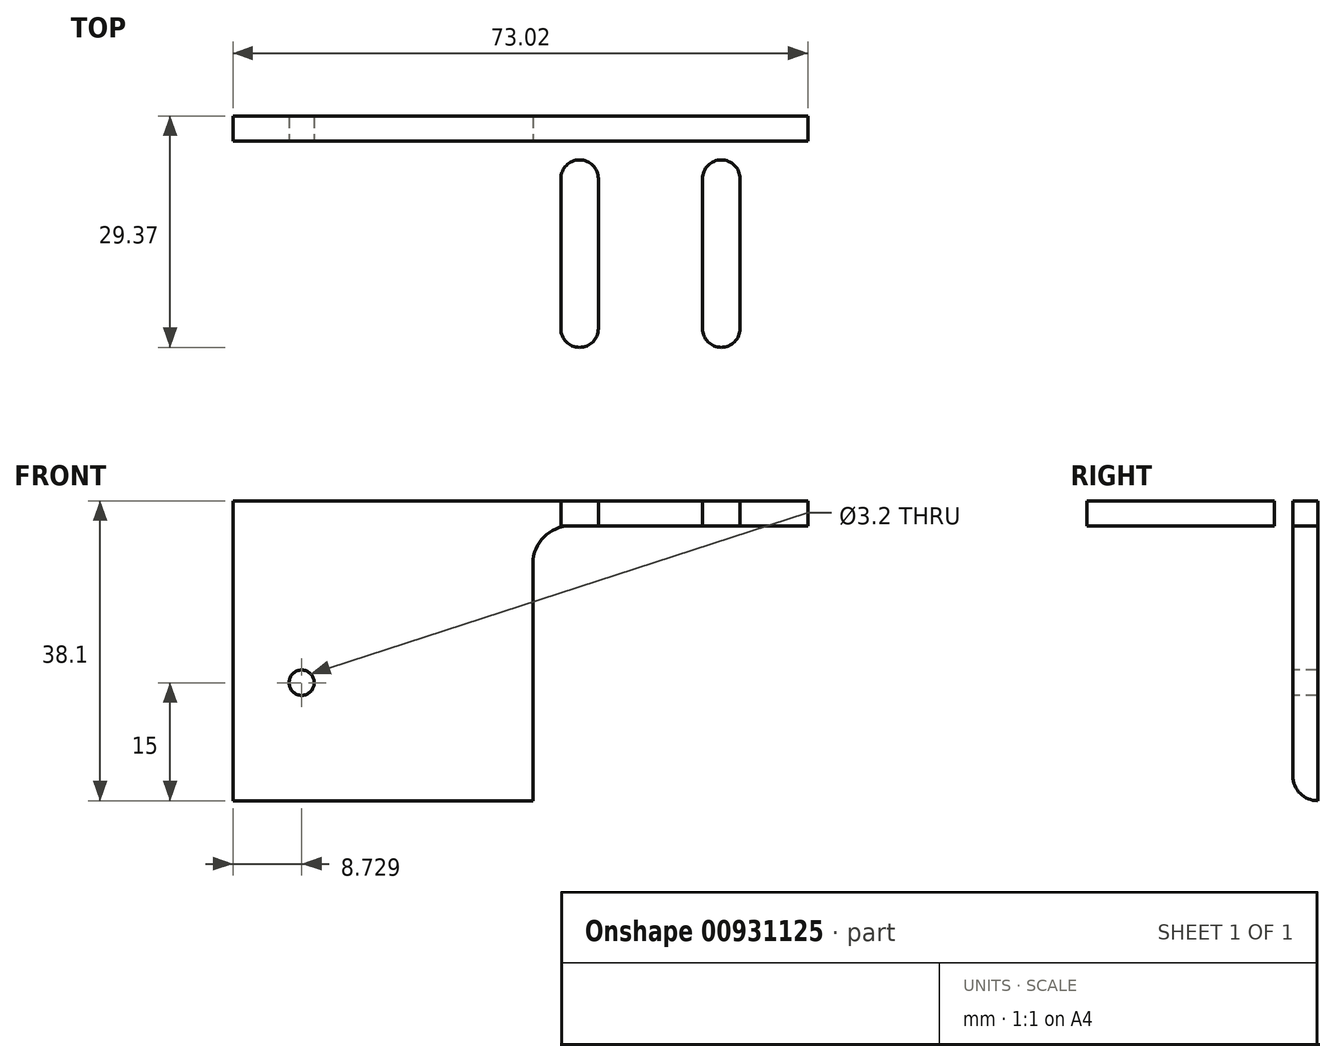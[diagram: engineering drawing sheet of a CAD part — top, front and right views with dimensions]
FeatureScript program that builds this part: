
annotation { "Feature Type Name" : "Feature", "Feature Type Description" : "" }
export const myFeature = defineFeature(function(context is Context, id is Id, definition is map)
    precondition{}
    {
        {
            var Q0;
            Q0=qCreatedBy(makeId("Front.planeOp"),FACE);
            var sketch = newSketch(context, id + "F0", { "sketchPlane" : qUnion([Q0])});
            skLineSegment(sketch, "E0.bottom", {"start": v(36.51, -19.05) * mm, "end": v(-36.51, -19.05) * mm});
            skLineSegment(sketch, "E0.top", {"start": v(36.51, 19.05) * mm, "end": v(-36.51, 19.05) * mm});
            skLineSegment(sketch, "E0.left", {"start": v(36.51, -19.05) * mm, "end": v(36.51, 19.05) * mm});
            skLineSegment(sketch, "E0.right", {"start": v(-36.51, -19.05) * mm, "end": v(-36.51, 19.05) * mm});
            skPoint(sketch, "E0.middle", {"position": v(0, 0) * mm});
            skSolve(sketch);
        }
        {
            var Q0;
            Q0=makeQuery(id+"F0.imprint","IMPRINT",FACE,{"disambiguationData":[TD([[makeQuery(id+"F0.imprint","IMPRINT",EDGE,{"derivedFrom":sQuery(id+"F0.wireOp",EDGE,"E0.bottom")}),-1.0]])]});
            extrude(context, id + "F1", {"entities" : qUnion([Q0]), "depth" : 3.17 * mm, "offsetDistance" : 25.4 * mm});
        }
        {
            var Q0;
            Q0=makeQuery(id+"F1.opExtrude","SWEPT_FACE",FACE,{"disambiguationData":[OSD([sQuery(id+"F0.wireOp",EDGE,"E0.top")])]});
            var sketch = newSketch(context, id + "F2", { "sketchPlane" : qUnion([Q0])});
            skLineSegment(sketch, "E1.bottom", {"start": v(-36.51, 0) * mm, "end": v(36.51, 0) * mm});
            skLineSegment(sketch, "E1.top", {"start": v(-36.51, -38.1) * mm, "end": v(36.51, -38.1) * mm});
            skLineSegment(sketch, "E1.left", {"start": v(-36.51, 0) * mm, "end": v(-36.51, -38.1) * mm});
            skLineSegment(sketch, "E1.right", {"start": v(36.51, 0) * mm, "end": v(36.51, -38.1) * mm});
            skSolve(sketch);
        }
        {
            var Q0;
            {var subQ0=sQuery(id+"F2.wireOp",EDGE,"E1.top");Q0=makeQuery(id+"F2.imprint","IMPRINT",FACE,{"disambiguationData":[TD([[makeQuery(id+"F2.imprint","IMPRINT",EDGE,{"derivedFrom":subQ0}),1.0]])]});}
            extrude(context, id + "F3", {"entities" : qUnion([Q0]), "operationType" : NewBodyOperationType.ADD, "oppositeDirection" : true, "depth" : 3.17 * mm, "offsetDistance" : 25.4 * mm});
        }
        {
            var Q0;
            Q0=makeQuery(id+"F1.opExtrude","CAP_FACE",FACE,{"disambiguationData":[OSD([sQuery(id+"F0.wireOp",EDGE,"E0.bottom"),sQuery(id+"F0.wireOp",EDGE,"E0.top"),sQuery(id+"F0.wireOp",EDGE,"E0.left"),sQuery(id+"F0.wireOp",EDGE,"E0.right")])],"isStart":false});
            var sketch = newSketch(context, id + "F4", { "sketchPlane" : qUnion([Q0])});
            skPoint(sketch, "E2", {"position": v(-27.78, -4.05) * mm});
            skSolve(sketch);
        }
        {
            var Q0;
            Q0=sQuery(id+"F4.wireOp",VERTEX,"E2");
            var Q1;
            Q1=makeQuery(id+"F1.opExtrude","SWEPT_BODY",BODY,{"disambiguationData":[OSD([sQuery(id+"F0.wireOp",EDGE,"E0.bottom"),sQuery(id+"F0.wireOp",EDGE,"E0.top"),sQuery(id+"F0.wireOp",EDGE,"E0.left"),sQuery(id+"F0.wireOp",EDGE,"E0.right")])]});
            hole(context, id + "F5", {"style" : HoleStyle.SIMPLE, "endStyle" : HoleEndStyle.BLIND, "standardTappedOrClearance" : lookupTablePath({ "fit" : "Close", "standard" : "ISO", "size" : "M3", "type" : "Clearance" }), "standardBlindInLast" : lookupTablePath({ "fit" : "Close", "standard" : "ISO", "engagement" : "75%", "pitch" : "0.5 mm", "size" : "M3", "type" : "Clearance & tapped" }), "holeDiameter" : 3.2 * mm, "majorDiameter" : 6.35 * mm, "holeDepth" : 34.92 * mm, "isTappedThrough" : true, "tappedDepth" : 7.9 * mm, "tapClearance" : 3, "startFromSketch" : true, "locations" : qUnion([Q0]), "scope" : qUnion([Q1])});
        }
        {
            var Q0;
            Q0=makeQuery(id+"F3.opExtrude","CAP_FACE",FACE,{"disambiguationData":[OSD([sQuery(id+"F0.wireOp",EDGE,"E0.top"),sQuery(id+"F2.wireOp",EDGE,"E1.top"),sQuery(id+"F2.wireOp",EDGE,"E1.left"),sQuery(id+"F2.wireOp",EDGE,"E1.right")])],"isStart":false});
            var sketch = newSketch(context, id + "F6", { "sketchPlane" : qUnion([Q0])});
            skLineSegment(sketch, "E3", {"start": v(25.51, 7.94) * mm, "end": v(25.51, 26.99) * mm});
            skLineSegment(sketch, "E4", {"start": v(7.51, 7.94) * mm, "end": v(7.51, 26.99) * mm});
            skArc(sketch, "E5.0.startCap", {"start": v(27.9, 7.94) * mm, "mid": v(25.51, 5.56) * mm, "end": v(23.13, 7.94) * mm});
            skArc(sketch, "E5.0.endCap", {"start": v(23.13, 26.99) * mm, "mid": v(25.51, 29.37) * mm, "end": v(27.9, 26.99) * mm});
            skLineSegment(sketch, "E5.0.left", {"start": v(23.13, 7.94) * mm, "end": v(23.13, 26.99) * mm});
            skLineSegment(sketch, "E5.0.right", {"start": v(27.9, 7.94) * mm, "end": v(27.9, 26.99) * mm});
            skArc(sketch, "E5.1.startCap", {"start": v(9.9, 7.94) * mm, "mid": v(7.51, 5.56) * mm, "end": v(5.13, 7.94) * mm});
            skArc(sketch, "E5.1.endCap", {"start": v(5.13, 26.99) * mm, "mid": v(7.51, 29.37) * mm, "end": v(9.9, 26.99) * mm});
            skLineSegment(sketch, "E5.1.left", {"start": v(5.13, 7.94) * mm, "end": v(5.13, 26.99) * mm});
            skLineSegment(sketch, "E5.1.right", {"start": v(9.9, 7.94) * mm, "end": v(9.9, 26.99) * mm});
            skSolve(sketch);
        }
        {
            var Q0;
            Q0=makeQuery(id+"F6.imprint","IMPRINT",FACE,{"disambiguationData":[TD([[makeQuery(id+"F6.imprint","IMPRINT",EDGE,{"derivedFrom":sQuery(id+"F6.wireOp",EDGE,"E5.1.startCap")}),-1.0]])]});
            var Q1;
            Q1=makeQuery(id+"F6.imprint","IMPRINT",FACE,{"disambiguationData":[TD([[makeQuery(id+"F6.imprint","IMPRINT",EDGE,{"derivedFrom":sQuery(id+"F6.wireOp",EDGE,"E5.0.startCap")}),-1.0]])]});
            extrude(context, id + "F7", {"entities" : qUnion([Q0, Q1]), "operationType" : NewBodyOperationType.REMOVE, "endBound" : BoundingType.THROUGH_ALL, "oppositeDirection" : true, "depth" : 25.4 * mm, "offsetDistance" : 25.4 * mm});
        }
        {
            var Q0;
            Q0=makeQuery(id+"F1.opExtrude","CAP_FACE",FACE,{"disambiguationData":[OSD([sQuery(id+"F0.wireOp",EDGE,"E0.bottom"),sQuery(id+"F0.wireOp",EDGE,"E0.top"),sQuery(id+"F0.wireOp",EDGE,"E0.left"),sQuery(id+"F0.wireOp",EDGE,"E0.right")])],"isStart":false});
            var sketch = newSketch(context, id + "F8", { "sketchPlane" : qUnion([Q0])});
            skLineSegment(sketch, "E6.bottom", {"start": v(36.51, 15.88) * mm, "end": v(1.59, 15.88) * mm});
            skLineSegment(sketch, "E6.top", {"start": v(36.51, -19.05) * mm, "end": v(1.59, -19.05) * mm});
            skLineSegment(sketch, "E6.left", {"start": v(36.51, 15.88) * mm, "end": v(36.51, -19.05) * mm});
            skLineSegment(sketch, "E6.right", {"start": v(1.59, 15.88) * mm, "end": v(1.59, -19.05) * mm});
            skSolve(sketch);
        }
        {
            var Q0;
            Q0=makeQuery(id+"F8.imprint","IMPRINT",FACE,{"disambiguationData":[TD([[makeQuery(id+"F8.imprint","IMPRINT",EDGE,{"derivedFrom":sQuery(id+"F8.wireOp",EDGE,"E6.bottom")}),1.0]])]});
            extrude(context, id + "F9", {"entities" : qUnion([Q0]), "operationType" : NewBodyOperationType.REMOVE, "endBound" : BoundingType.THROUGH_ALL, "oppositeDirection" : true, "depth" : 25.4 * mm, "offsetDistance" : 25.4 * mm});
        }
        {
            var Q0;
            Q0=makeQuery(id+"F3.opExtrude","CAP_EDGE",EDGE,{"disambiguationData":[OSD([sQuery(id+"F2.wireOp",EDGE,"E1.top")])],"isStart":false});
            var Q1;
            Q1=makeQuery(id+"F1.opExtrude","CAP_EDGE",EDGE,{"disambiguationData":[OSD([sQuery(id+"F0.wireOp",EDGE,"E0.bottom")])],"isStart":false});
            fillet(context, id + "F10", {"entities" : qUnion([Q0, Q1]), "radius" : 3.17 * mm, "tangentPropagation" : true, "allowEdgeOverflow" : false});
        }
        {
            var Q0;
            Q0=makeQuery(id+"F9.boolean.opBoolean","COPY",EDGE,{"derivedFrom":makeQuery(id+"F9.opExtrude","SWEPT_EDGE",EDGE,{"disambiguationData":[OSD([sQuery(id+"F0.wireOp",EDGE,"E0.top"),sQuery(id+"F8.wireOp",EDGE,"E6.bottom"),sQuery(id+"F8.wireOp",EDGE,"E6.right")])]})});
            fillet(context, id + "F11", {"entities" : qUnion([Q0]), "radius" : 4.76 * mm, "tangentPropagation" : true, "allowEdgeOverflow" : false});
        }
    });
